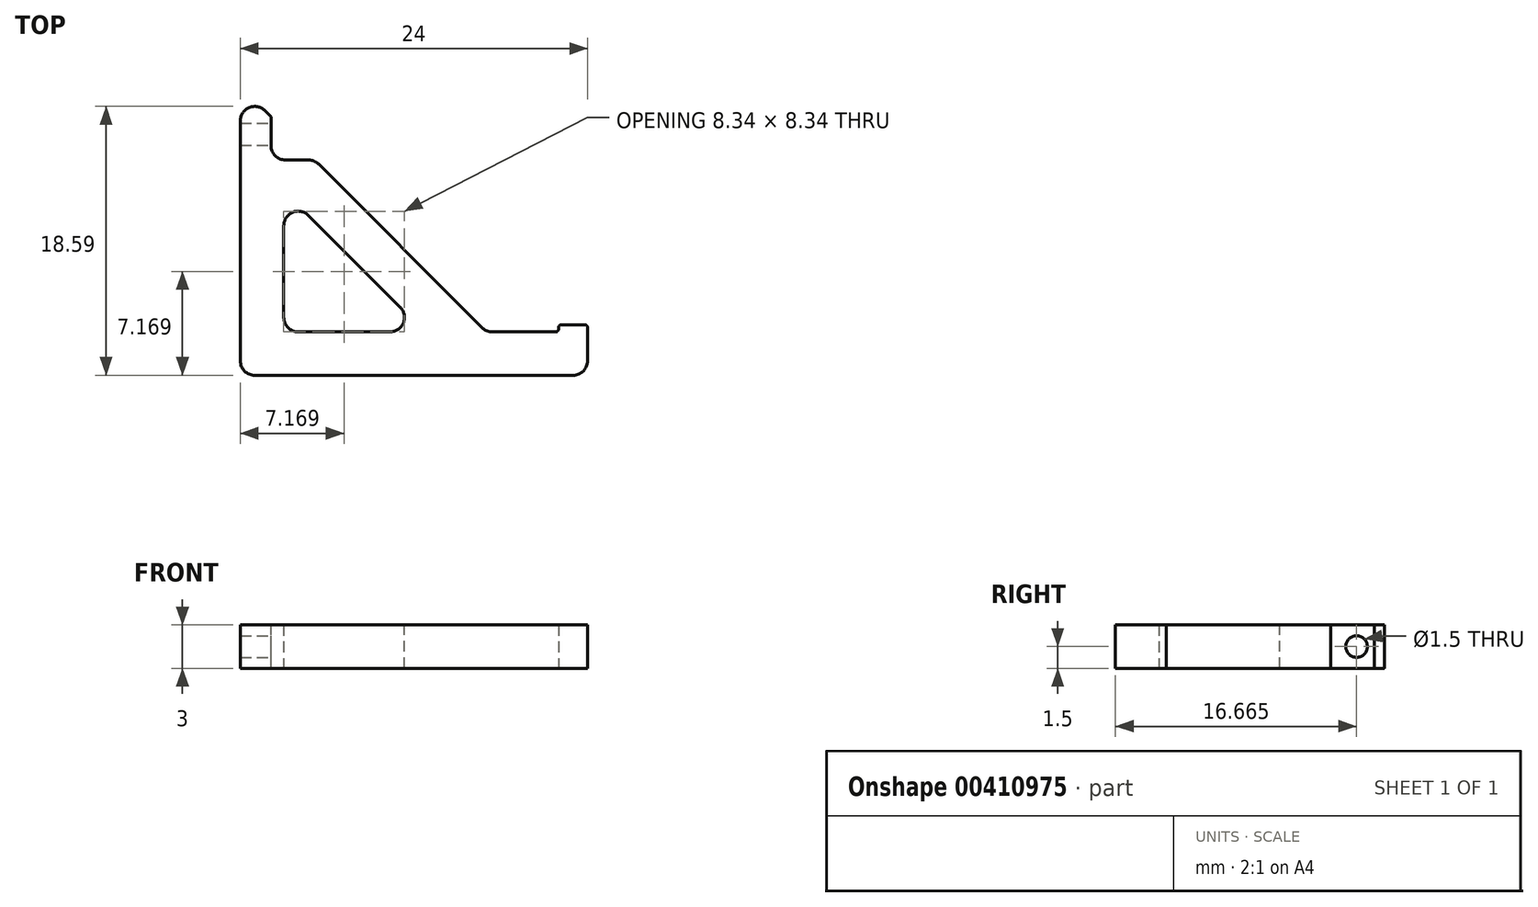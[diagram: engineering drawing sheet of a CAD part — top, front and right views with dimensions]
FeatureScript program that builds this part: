
annotation { "Feature Type Name" : "Feature", "Feature Type Description" : "" }
export const myFeature = defineFeature(function(context is Context, id is Id, definition is map)
    precondition{}
    {
        {
            var Q0;
            Q0=qCreatedBy(makeId("Top.planeOp"),FACE);
            var sketch = newSketch(context, id + "F0", { "sketchPlane" : qUnion([Q0])});
            skLineSegment(sketch, "E0", {"start": v(0, 20) * mm, "end": v(0, 0) * mm});
            skLineSegment(sketch, "E1", {"start": v(0, 0) * mm, "end": v(24, 0) * mm});
            skLineSegment(sketch, "E2", {"start": v(24, 0) * mm, "end": v(24, 3.5) * mm});
            skLineSegment(sketch, "E3", {"start": v(24, 3.5) * mm, "end": v(22, 3.5) * mm});
            skLineSegment(sketch, "E4", {"start": v(22, 3.5) * mm, "end": v(22, 3) * mm});
            skLineSegment(sketch, "E5", {"start": v(22, 3) * mm, "end": v(17, 3) * mm});
            skLineSegment(sketch, "E6", {"start": v(3, 3) * mm, "end": v(3, 12.76) * mm});
            skLineSegment(sketch, "E7", {"start": v(0, 20) * mm, "end": v(17, 3) * mm});
            skLineSegment(sketch, "E8", {"start": v(3, 12.76) * mm, "end": v(12.76, 3) * mm});
            skLineSegment(sketch, "E9.trimOffspring", {"start": v(12.76, 3) * mm, "end": v(3, 3) * mm});
            skSolve(sketch);
        }
        {
            var Q0;
            Q0=makeQuery(id+"F0.imprint","IMPRINT",FACE,{"disambiguationData":[TD([[makeQuery(id+"F0.imprint","IMPRINT",EDGE,{"derivedFrom":sQuery(id+"F0.wireOp",EDGE,"E0")}),1.0]])]});
            extrude(context, id + "F1", {"entities" : qUnion([Q0]), "depth" : 3 * mm});
        }
        {
            var Q0;
            Q0=makeQuery(id+"F1.opExtrude","CAP_FACE",FACE,{"disambiguationData":[OSD([sQuery(id+"F0.wireOp",EDGE,"E0"),sQuery(id+"F0.wireOp",EDGE,"E1"),sQuery(id+"F0.wireOp",EDGE,"E2"),sQuery(id+"F0.wireOp",EDGE,"E3"),sQuery(id+"F0.wireOp",EDGE,"E4"),sQuery(id+"F0.wireOp",EDGE,"E5"),sQuery(id+"F0.wireOp",EDGE,"E6"),sQuery(id+"F0.wireOp",EDGE,"E7"),sQuery(id+"F0.wireOp",EDGE,"E8"),sQuery(id+"F0.wireOp",EDGE,"E9.trimOffspring")])],"isStart":false});
            var sketch = newSketch(context, id + "F2", { "sketchPlane" : qUnion([Q0])});
            skLineSegment(sketch, "E10.bottom", {"start": v(2.12, 17.88) * mm, "end": v(5.12, 17.88) * mm});
            skLineSegment(sketch, "E10.top", {"start": v(2.12, 14.88) * mm, "end": v(5.12, 14.88) * mm});
            skLineSegment(sketch, "E10.left", {"start": v(2.12, 17.88) * mm, "end": v(2.12, 14.88) * mm});
            skLineSegment(sketch, "E10.right", {"start": v(5.12, 17.88) * mm, "end": v(5.12, 14.88) * mm});
            skSolve(sketch);
        }
        {
            var Q0;
            {var subQ0=sQuery(id+"F2.wireOp",EDGE,"E10.bottom");Q0=makeQuery(id+"F2.imprint","IMPRINT",FACE,{"disambiguationData":[TD([[makeQuery(id+"F2.imprint","IMPRINT",EDGE,{"derivedFrom":subQ0}),-1.0]])]});}
            var Q1;
            {var subQ0=sQuery(id+"F2.wireOp",EDGE,"E10.top");Q1=makeQuery(id+"F2.imprint","IMPRINT",FACE,{"disambiguationData":[TD([[makeQuery(id+"F2.imprint","IMPRINT",EDGE,{"derivedFrom":subQ0}),1.0]])]});}
            extrude(context, id + "F3", {"entities" : qUnion([Q0, Q1]), "operationType" : NewBodyOperationType.REMOVE, "endBound" : BoundingType.THROUGH_ALL, "oppositeDirection" : true, "depth" : 25 * mm});
        }
        {
            var Q0;
            Q0=makeQuery(id+"F3.boolean.opBoolean","COPY",EDGE,{"derivedFrom":makeQuery(id+"F3.opExtrude","SWEPT_EDGE",EDGE,{"disambiguationData":[OSD([sQuery(id+"F0.wireOp",EDGE,"E7"),sQuery(id+"F2.wireOp",EDGE,"E10.top"),sQuery(id+"F2.wireOp",EDGE,"E10.right")])]})});
            var Q1;
            Q1=makeQuery(id+"F3.boolean.opBoolean","COPY",EDGE,{"derivedFrom":makeQuery(id+"F3.opExtrude","SWEPT_EDGE",EDGE,{"disambiguationData":[OSD([sQuery(id+"F2.wireOp",EDGE,"E10.top"),sQuery(id+"F2.wireOp",EDGE,"E10.left")])]})});
            var Q2;
            Q2=makeQuery(id+"F1.opExtrude","SWEPT_EDGE",EDGE,{"disambiguationData":[OSD([sQuery(id+"F0.wireOp",EDGE,"E6"),sQuery(id+"F0.wireOp",EDGE,"E8")])]});
            var Q3;
            Q3=makeQuery(id+"F1.opExtrude","SWEPT_EDGE",EDGE,{"disambiguationData":[OSD([sQuery(id+"F0.wireOp",EDGE,"E5"),sQuery(id+"F0.wireOp",EDGE,"E7")])]});
            var Q4;
            Q4=makeQuery(id+"F1.opExtrude","SWEPT_EDGE",EDGE,{"disambiguationData":[OSD([sQuery(id+"F0.wireOp",EDGE,"E6"),sQuery(id+"F0.wireOp",EDGE,"E9.trimOffspring")])]});
            var Q5;
            Q5=makeQuery(id+"F1.opExtrude","SWEPT_EDGE",EDGE,{"disambiguationData":[OSD([sQuery(id+"F0.wireOp",EDGE,"E8"),sQuery(id+"F0.wireOp",EDGE,"E9.trimOffspring")])]});
            var Q6;
            Q6=makeQuery(id+"F3.boolean.opBoolean","COPY",EDGE,{"derivedFrom":makeQuery(id+"F3.opExtrude","SWEPT_EDGE",EDGE,{"disambiguationData":[OSD([sQuery(id+"F0.wireOp",EDGE,"E7"),sQuery(id+"F2.wireOp",EDGE,"E10.bottom"),sQuery(id+"F2.wireOp",EDGE,"E10.left")])]})});
            var Q7;
            Q7=makeQuery(id+"F1.opExtrude","SWEPT_EDGE",EDGE,{"disambiguationData":[OSD([sQuery(id+"F0.wireOp",EDGE,"E1"),sQuery(id+"F0.wireOp",EDGE,"E2")])]});
            var Q8;
            Q8=makeQuery(id+"F1.opExtrude","SWEPT_EDGE",EDGE,{"disambiguationData":[OSD([sQuery(id+"F0.wireOp",EDGE,"E0"),sQuery(id+"F0.wireOp",EDGE,"E7")])]});
            var Q9;
            Q9=makeQuery(id+"F1.opExtrude","SWEPT_EDGE",EDGE,{"disambiguationData":[OSD([sQuery(id+"F0.wireOp",EDGE,"E0"),sQuery(id+"F0.wireOp",EDGE,"E1")])]});
            fillet(context, id + "F4", {"entities" : qUnion([Q0, Q1, Q2, Q3, Q4, Q5, Q6, Q7, Q8, Q9]), "radius" : 1 * mm, "tangentPropagation" : true, "allowEdgeOverflow" : false});
        }
        {
            var Q0;
            Q0=makeQuery(id+"F1.opExtrude","SWEPT_EDGE",EDGE,{"disambiguationData":[OSD([sQuery(id+"F0.wireOp",EDGE,"E4"),sQuery(id+"F0.wireOp",EDGE,"E5")])]});
            var Q1;
            Q1=makeQuery(id+"F1.opExtrude","SWEPT_EDGE",EDGE,{"disambiguationData":[OSD([sQuery(id+"F0.wireOp",EDGE,"E2"),sQuery(id+"F0.wireOp",EDGE,"E3")])]});
            var Q2;
            Q2=makeQuery(id+"F1.opExtrude","SWEPT_EDGE",EDGE,{"disambiguationData":[OSD([sQuery(id+"F0.wireOp",EDGE,"E3"),sQuery(id+"F0.wireOp",EDGE,"E4")])]});
            fillet(context, id + "F5", {"entities" : qUnion([Q0, Q1, Q2]), "radius" : 0.2 * mm, "tangentPropagation" : true, "allowEdgeOverflow" : false});
        }
        {
            var Q0;
            Q0=makeQuery(id+"F3.boolean.opBoolean","COPY",FACE,{"derivedFrom":makeQuery(id+"F3.opExtrude","SWEPT_FACE",FACE,{"disambiguationData":[OSD([sQuery(id+"F2.wireOp",EDGE,"E10.left")])]})});
            var sketch = newSketch(context, id + "F6", { "sketchPlane" : qUnion([Q0])});
            skCircle(sketch, "E11", {"center": v(16.66, 1.5) * mm, "radius": 0.75 * mm});
            skSolve(sketch);
        }
        {
            var Q0;
            Q0=makeQuery(id+"F6.imprint","IMPRINT",FACE,{"disambiguationData":[TD([[makeQuery(id+"F6.imprint","IMPRINT",EDGE,{"derivedFrom":sQuery(id+"F6.wireOp",EDGE,"E11")}),1.0]])]});
            extrude(context, id + "F7", {"entities" : qUnion([Q0]), "operationType" : NewBodyOperationType.REMOVE, "endBound" : BoundingType.THROUGH_ALL, "oppositeDirection" : true, "depth" : 25 * mm});
        }
    });
